# Revit family: Haworth_EncloseFrameless_Wall_GlassCorner
name_source: partatom
category: Furniture Systems
revit_build: Autodesk Revit 2018 (Build: 20170223_1515(x64)
units: mm (PartAtom-declared; Revit-internal decimal feet)

## family parameters
Always vertical = Yes
Cut with Voids When Loaded = No
OmniClass Number = 23.25.40.14
OmniClass Title = Demountable Partitions
Part Type = Normal
Room Calculation Point = No
Round Connector Dimension = Use Diameter
Shared = Yes
Work Plane-Based = No

## types (2) — shared parameters
Actual Height = 108 "
Assembly Code = C1010200
Base Height = 1.25 "
Cap Height = 1 "
Ceiling Mount = Yes
Description = Wall-Glass_Corner
End of Run Finish = Haworth _ Polymer _ Black
Frame Depth = 4 "
Frame Finish = Haworth _ Metal _ Brushed Aluminum
Glass Finish = Haworth _ Glass _ Clear
Glazing Connector = No
Glazing Connector_135 = No
Glazing Connector_90 = No
Half Postcap Width = 0.155 "
Height = 108 "
Horizontal Bottom Adjuster Width = 2.125 "
Horizontal Bottom Trim Width = 2.425 "
Horizontal Frame Width = 0.875 "
Horizontal Top Adjuster Width = 2.625 "
Horizontal Top Trim Width = 1.43 "
Manufacturer = Haworth
Material Options = http://surfaces.haworth.com
Max. Height = 144 "
Min. Height = 24 "
Min/Max Height = 24-144 in.
Min/Max Width = 12in Min, Verify Max
Model = Haworth - Enclose Frameless
Panel Depth = 0.4 "
Panel Height = 101.5 "
Revision Number = 3
Size = Verify Final Dim. w/ Haworth
Sustainability Info = http://www.haworth.com
URL = www.haworth.com
URL - Product = http://www.haworth.com
Vertical Frame Width = 0.875 "
Warranty = http://www.haworth.com

## per-type parameters (varying)
| type | 135 Degree | 90 Degree | Angle | Cut Angle |
| 108"_135 Degree | Yes | No | 135.00° | 67.50° |
| 108"_90 Degree | No | Yes | 90.00° | 45.00° |

## geometry (parser evidence)
native form markers: Sweep x15
no freeform markers — native parametric forms only
